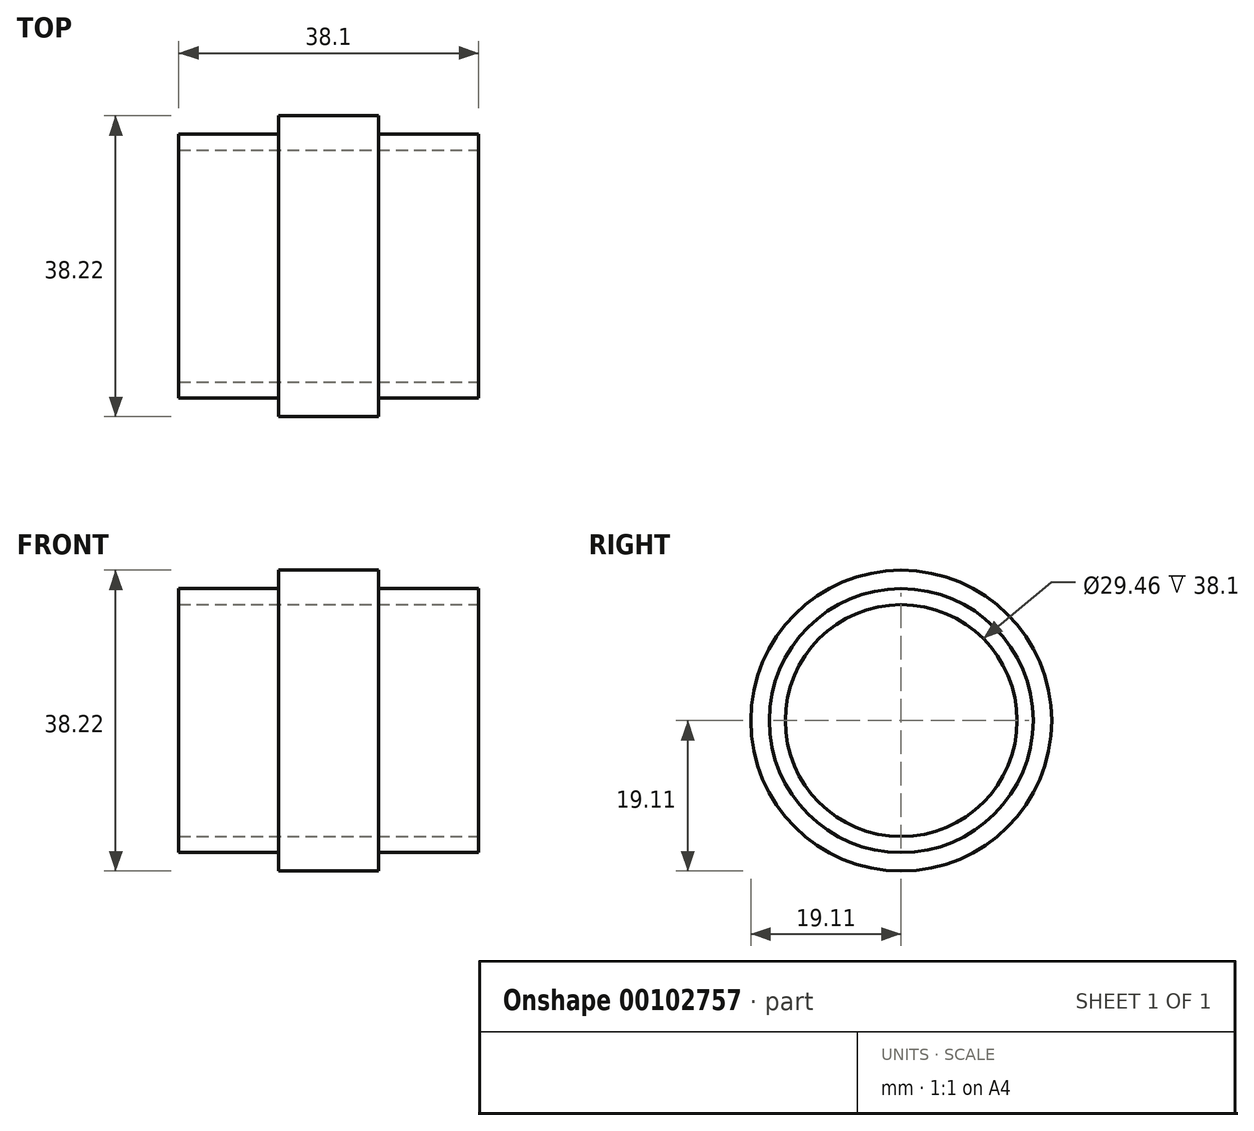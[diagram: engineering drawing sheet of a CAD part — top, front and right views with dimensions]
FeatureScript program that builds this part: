
annotation { "Feature Type Name" : "Feature", "Feature Type Description" : "" }
export const myFeature = defineFeature(function(context is Context, id is Id, definition is map)
    precondition{}
    {
        {
            var Q0;
            Q0=qCreatedBy(makeId("Front.planeOp"),FACE);
            var sketch = newSketch(context, id + "F0", { "sketchPlane" : qUnion([Q0])});
            skLineSegment(sketch, "E0.bottom", {"start": v(-19.05, 14.73) * mm, "end": v(19.05, 14.73) * mm});
            skLineSegment(sketch, "E0.top", {"start": v(-19.05, 16.76) * mm, "end": v(-6.35, 16.76) * mm});
            skLineSegment(sketch, "E0.left", {"start": v(-19.05, 14.73) * mm, "end": v(-19.05, 16.76) * mm});
            skLineSegment(sketch, "E0.right", {"start": v(19.05, 14.73) * mm, "end": v(19.05, 16.76) * mm});
            skLineSegment(sketch, "E1.top", {"start": v(-6.35, 19.11) * mm, "end": v(6.35, 19.11) * mm});
            skLineSegment(sketch, "E1.left", {"start": v(-6.35, 16.76) * mm, "end": v(-6.35, 19.11) * mm});
            skLineSegment(sketch, "E1.right", {"start": v(6.35, 16.76) * mm, "end": v(6.35, 19.11) * mm});
            skLineSegment(sketch, "E2.trimOffspring", {"start": v(6.35, 16.76) * mm, "end": v(19.05, 16.76) * mm});
            skLineSegment(sketch, "E3", {"start": v(18.5, 0) * mm, "end": v(-25.91, 0) * mm});
            skSolve(sketch);
        }
        {
            var Q0;
            Q0=makeQuery(id+"F0.imprint","IMPRINT",FACE,{"disambiguationData":[TD([[makeQuery(id+"F0.imprint","IMPRINT",EDGE,{"derivedFrom":sQuery(id+"F0.wireOp",EDGE,"E0.bottom")}),1.0]])]});
            var Q1;
            Q1=sQuery(id+"F0.wireOp",EDGE,"E3");
            revolve(context, id + "F1", {"entities" : qUnion([Q0]), "axis" : qUnion([Q1]), "revolveType" : RevolveType.FULL});
        }
    });
